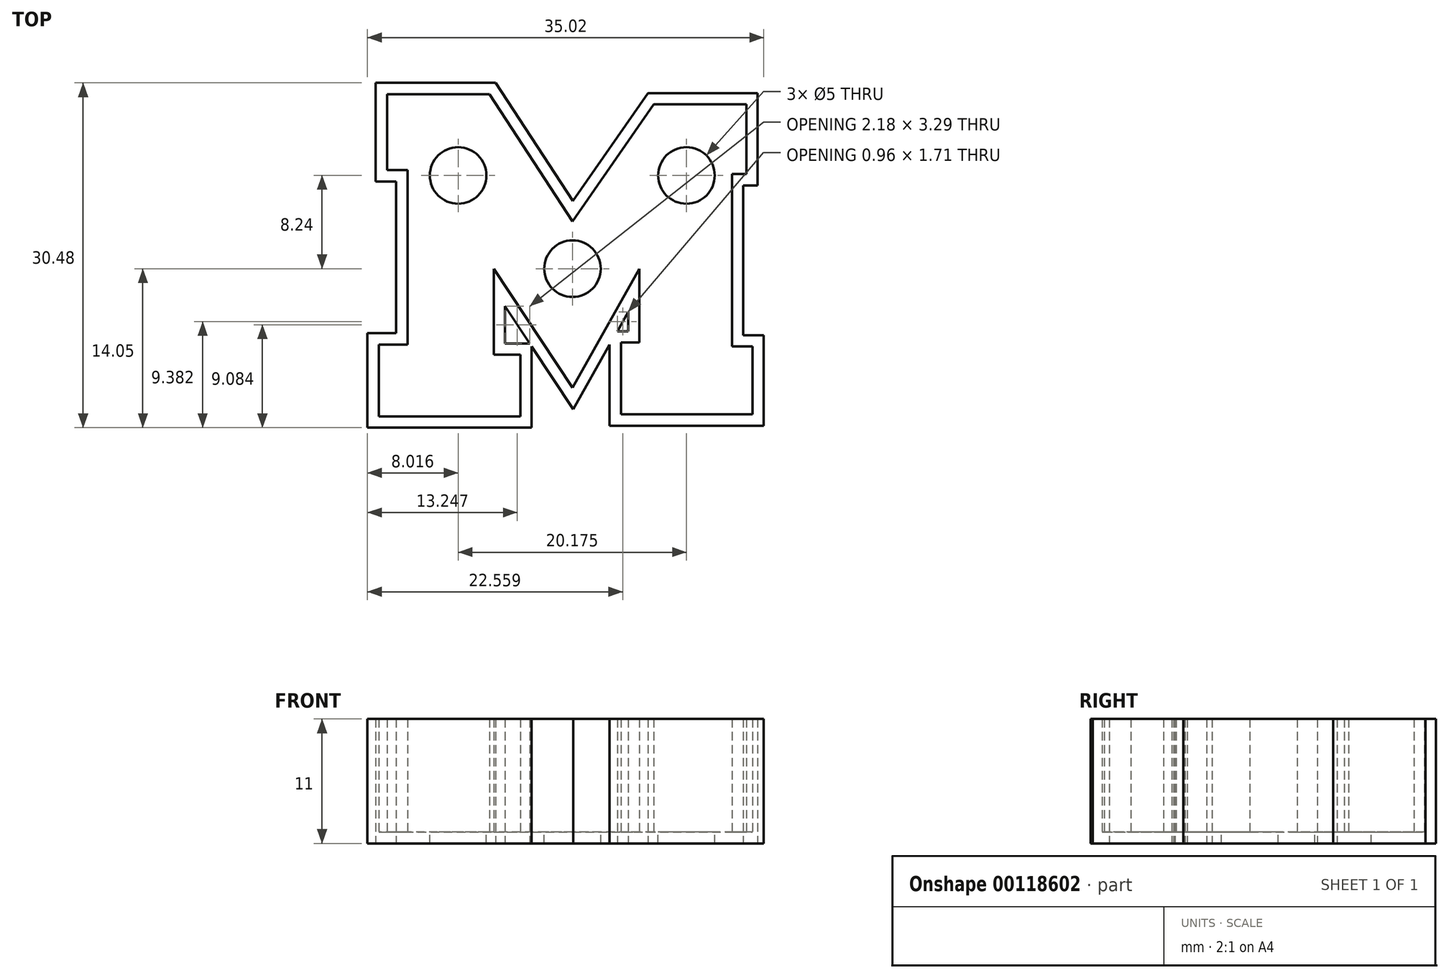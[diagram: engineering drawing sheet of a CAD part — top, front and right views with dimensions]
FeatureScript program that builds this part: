
annotation { "Feature Type Name" : "Feature", "Feature Type Description" : "" }
export const myFeature = defineFeature(function(context is Context, id is Id, definition is map)
    precondition{}
    {
        {
            var Q0;
            Q0=qCreatedBy(makeId("Top.planeOp"),FACE);
            var sketch = newSketch(context, id + "F0", { "sketchPlane" : qUnion([Q0])});
            skLineSegment(sketch, "E0", {"start": v(-14.58, 8.72) * mm, "end": v(-14.58, -6.7) * mm});
            skLineSegment(sketch, "E1", {"start": v(-14.58, -6.7) * mm, "end": v(-17.12, -6.7) * mm});
            skLineSegment(sketch, "E2", {"start": v(-17.12, -6.7) * mm, "end": v(-17.12, -13.05) * mm});
            skLineSegment(sketch, "E3", {"start": v(-17.12, -13.05) * mm, "end": v(-4.6, -13.05) * mm});
            skLineSegment(sketch, "E4", {"start": v(-4.6, -13.05) * mm, "end": v(-4.6, -7.61) * mm});
            skLineSegment(sketch, "E5", {"start": v(-4.6, -7.61) * mm, "end": v(-6.96, -7.61) * mm});
            skLineSegment(sketch, "E6", {"start": v(-6.96, -7.61) * mm, "end": v(-6.96, 0) * mm});
            skLineSegment(sketch, "E7", {"start": v(-6.96, 0) * mm, "end": v(0, -10.51) * mm});
            skLineSegment(sketch, "E8", {"start": v(0, -10.51) * mm, "end": v(5.92, 0) * mm});
            skLineSegment(sketch, "E9", {"start": v(5.92, 0) * mm, "end": v(5.92, -6.52) * mm});
            skLineSegment(sketch, "E10", {"start": v(5.92, -6.52) * mm, "end": v(4.29, -6.52) * mm});
            skLineSegment(sketch, "E11", {"start": v(4.29, -6.52) * mm, "end": v(4.29, -12.87) * mm});
            skLineSegment(sketch, "E12", {"start": v(4.29, -12.87) * mm, "end": v(15.9, -12.87) * mm});
            skLineSegment(sketch, "E13", {"start": v(15.9, -12.87) * mm, "end": v(15.9, -6.88) * mm});
            skLineSegment(sketch, "E14", {"start": v(15.9, -6.88) * mm, "end": v(14.08, -6.88) * mm});
            skLineSegment(sketch, "E15", {"start": v(14.08, -6.88) * mm, "end": v(14.08, 8.36) * mm});
            skLineSegment(sketch, "E16", {"start": v(14.08, 8.36) * mm, "end": v(15.35, 8.36) * mm});
            skLineSegment(sketch, "E17", {"start": v(15.35, 8.36) * mm, "end": v(15.35, 14.52) * mm});
            skLineSegment(sketch, "E18", {"start": v(15.35, 14.52) * mm, "end": v(7.19, 14.52) * mm});
            skLineSegment(sketch, "E19", {"start": v(7.19, 14.52) * mm, "end": v(0, 4.18) * mm});
            skLineSegment(sketch, "E20", {"start": v(0, 4.18) * mm, "end": v(-7.33, 15.43) * mm});
            skLineSegment(sketch, "E21", {"start": v(-7.33, 15.43) * mm, "end": v(-16.4, 15.43) * mm});
            skLineSegment(sketch, "E22", {"start": v(-16.4, 15.43) * mm, "end": v(-16.4, 8.72) * mm});
            skLineSegment(sketch, "E23", {"start": v(-16.4, 8.72) * mm, "end": v(-14.58, 8.72) * mm});
            skSolve(sketch);
        }
        {
            var Q0;
            Q0=makeQuery(id+"F0.imprint","IMPRINT",FACE,{"disambiguationData":[TD([[makeQuery(id+"F0.imprint","IMPRINT",EDGE,{"derivedFrom":sQuery(id+"F0.wireOp",EDGE,"E0")}),1.0]])]});
            extrude(context, id + "F1", {"entities" : qUnion([Q0]), "depth" : 10 * mm});
        }
        {
            var Q0;
            Q0=makeQuery(id+"F1.opExtrude","CAP_FACE",FACE,{"disambiguationData":[OSD([sQuery(id+"F0.wireOp",EDGE,"E0"),sQuery(id+"F0.wireOp",EDGE,"E1"),sQuery(id+"F0.wireOp",EDGE,"E2"),sQuery(id+"F0.wireOp",EDGE,"E3"),sQuery(id+"F0.wireOp",EDGE,"E4"),sQuery(id+"F0.wireOp",EDGE,"E5"),sQuery(id+"F0.wireOp",EDGE,"E6"),sQuery(id+"F0.wireOp",EDGE,"E7"),sQuery(id+"F0.wireOp",EDGE,"E8"),sQuery(id+"F0.wireOp",EDGE,"E9"),sQuery(id+"F0.wireOp",EDGE,"E10"),sQuery(id+"F0.wireOp",EDGE,"E11"),sQuery(id+"F0.wireOp",EDGE,"E12"),sQuery(id+"F0.wireOp",EDGE,"E13"),sQuery(id+"F0.wireOp",EDGE,"E14"),sQuery(id+"F0.wireOp",EDGE,"E15"),sQuery(id+"F0.wireOp",EDGE,"E16"),sQuery(id+"F0.wireOp",EDGE,"E17"),sQuery(id+"F0.wireOp",EDGE,"E18"),sQuery(id+"F0.wireOp",EDGE,"E19"),sQuery(id+"F0.wireOp",EDGE,"E20"),sQuery(id+"F0.wireOp",EDGE,"E21"),sQuery(id+"F0.wireOp",EDGE,"E22"),sQuery(id+"F0.wireOp",EDGE,"E23")])],"isStart":false});
            shell(context, id + "F2", {"entities" : qUnion([Q0]), "thickness" : 1 * mm, "oppositeDirection" : true});
        }
        {
            var Q0;
            Q0=makeQuery(id+"F2.opShell","OFFSET_FACE",FACE,{"disambiguationData":[OSD([sQuery(id+"F0.wireOp",EDGE,"E0"),sQuery(id+"F0.wireOp",EDGE,"E1"),sQuery(id+"F0.wireOp",EDGE,"E2"),sQuery(id+"F0.wireOp",EDGE,"E3"),sQuery(id+"F0.wireOp",EDGE,"E4"),sQuery(id+"F0.wireOp",EDGE,"E5"),sQuery(id+"F0.wireOp",EDGE,"E6"),sQuery(id+"F0.wireOp",EDGE,"E7"),sQuery(id+"F0.wireOp",EDGE,"E8"),sQuery(id+"F0.wireOp",EDGE,"E9"),sQuery(id+"F0.wireOp",EDGE,"E10"),sQuery(id+"F0.wireOp",EDGE,"E11"),sQuery(id+"F0.wireOp",EDGE,"E12"),sQuery(id+"F0.wireOp",EDGE,"E13"),sQuery(id+"F0.wireOp",EDGE,"E14"),sQuery(id+"F0.wireOp",EDGE,"E15"),sQuery(id+"F0.wireOp",EDGE,"E16"),sQuery(id+"F0.wireOp",EDGE,"E17"),sQuery(id+"F0.wireOp",EDGE,"E18"),sQuery(id+"F0.wireOp",EDGE,"E19"),sQuery(id+"F0.wireOp",EDGE,"E20"),sQuery(id+"F0.wireOp",EDGE,"E21"),sQuery(id+"F0.wireOp",EDGE,"E22"),sQuery(id+"F0.wireOp",EDGE,"E23")])]});
            var sketch = newSketch(context, id + "F3", { "sketchPlane" : qUnion([Q0])});
            skCircle(sketch, "E24", {"center": v(0, 0) * mm, "radius": 3.21 * mm});
            skCircle(sketch, "E25", {"center": v(10.07, 8.24) * mm, "radius": 3.1 * mm});
            skCircle(sketch, "E26", {"center": v(-10.1, 8.24) * mm, "radius": 2.8 * mm});
            skSolve(sketch);
        }
        {
            var Q0;
            Q0=sQuery(id+"F3.wireOp",VERTEX,"E24.center");
            var Q1;
            Q1=sQuery(id+"F3.wireOp",VERTEX,"E25.center");
            var Q2;
            Q2=sQuery(id+"F3.wireOp",VERTEX,"E26.center");
            var Q3;
            Q3=makeQuery(id+"F1.opExtrude","SWEPT_BODY",BODY,{"disambiguationData":[OSD([sQuery(id+"F0.wireOp",EDGE,"E0"),sQuery(id+"F0.wireOp",EDGE,"E1"),sQuery(id+"F0.wireOp",EDGE,"E2"),sQuery(id+"F0.wireOp",EDGE,"E3"),sQuery(id+"F0.wireOp",EDGE,"E4"),sQuery(id+"F0.wireOp",EDGE,"E5"),sQuery(id+"F0.wireOp",EDGE,"E6"),sQuery(id+"F0.wireOp",EDGE,"E7"),sQuery(id+"F0.wireOp",EDGE,"E8"),sQuery(id+"F0.wireOp",EDGE,"E9"),sQuery(id+"F0.wireOp",EDGE,"E10"),sQuery(id+"F0.wireOp",EDGE,"E11"),sQuery(id+"F0.wireOp",EDGE,"E12"),sQuery(id+"F0.wireOp",EDGE,"E13"),sQuery(id+"F0.wireOp",EDGE,"E14"),sQuery(id+"F0.wireOp",EDGE,"E15"),sQuery(id+"F0.wireOp",EDGE,"E16"),sQuery(id+"F0.wireOp",EDGE,"E17"),sQuery(id+"F0.wireOp",EDGE,"E18"),sQuery(id+"F0.wireOp",EDGE,"E19"),sQuery(id+"F0.wireOp",EDGE,"E20"),sQuery(id+"F0.wireOp",EDGE,"E21"),sQuery(id+"F0.wireOp",EDGE,"E22"),sQuery(id+"F0.wireOp",EDGE,"E23")])]});
            hole(context, id + "F4", {"style" : HoleStyle.SIMPLE, "endStyle" : HoleEndStyle.THROUGH, "holeDiameter" : 5 * mm, "locations" : qUnion([Q0, Q1, Q2]), "scope" : qUnion([Q3]), "isTappedThrough" : true});
        }
    });
